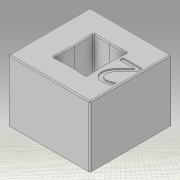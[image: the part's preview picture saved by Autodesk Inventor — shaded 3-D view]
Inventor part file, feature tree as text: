
AUTODESK INVENTOR PART (.ipt)
format: ipt  version: 2018 (Build 220112000, 112)  size: 223,232 bytes
history: native  units: in
note: dims shown in document units (in); Inventor stores cm internally (conversion verified against a paired STEP export)
features: extrude x5, sketch x5, plane x2, mirror x2, fillet x2, projected_geometry x2
ambient origin geometry x8: Origin, YZ Plane, XZ Plane, XY Plane, X Axis, Y Axis, Z Axis, Center Point
bodies: Solid1 (feature_tree)
feature tree (18):
  extrude  "Extrusion1"  Depth=2.0in
  extrude  "Extrusion2"  Depth=0.525in
  extrude  "Extrusion3"  Depth=0.941in
  plane  "Work Plane1"
  plane  "Work Plane2"
  mirror  "Mirror1"
  mirror  "Mirror2"
  fillet  "Fillet1"  Radius=0.911in
  fillet  "Fillet2"  Radius=0.05in
  extrude  "Extrusion4"  Depth=0.05in
  extrude  "Extrusion5"  Depth=0.941in TaperAngle=0.0deg
  sketch  "Sketch1"  dims[d0=2.0in d1=2.0in]
  sketch  "Sketch2"  dims[d2=1.5in d3=0.0in d5=0.525in]
  projected_geometry  "Projected Loop1"
  sketch  "Sketch3"  dims[d6=0.755in d7=0.941in d8=0.911in d9=0.0in d10=0.05in]
  sketch  "Sketch4"  dims[d11=0.05in d12=0.05in]
  sketch  "Sketch5"  dims[d13=0.05in d14=0.941in d15=0.0in d16=0.025in d17=0.025in d18=0.025in d19=0.0in d20=0.515in d21=1.0in d22=0.0in]
  projected_geometry  "Projected Loop2"
